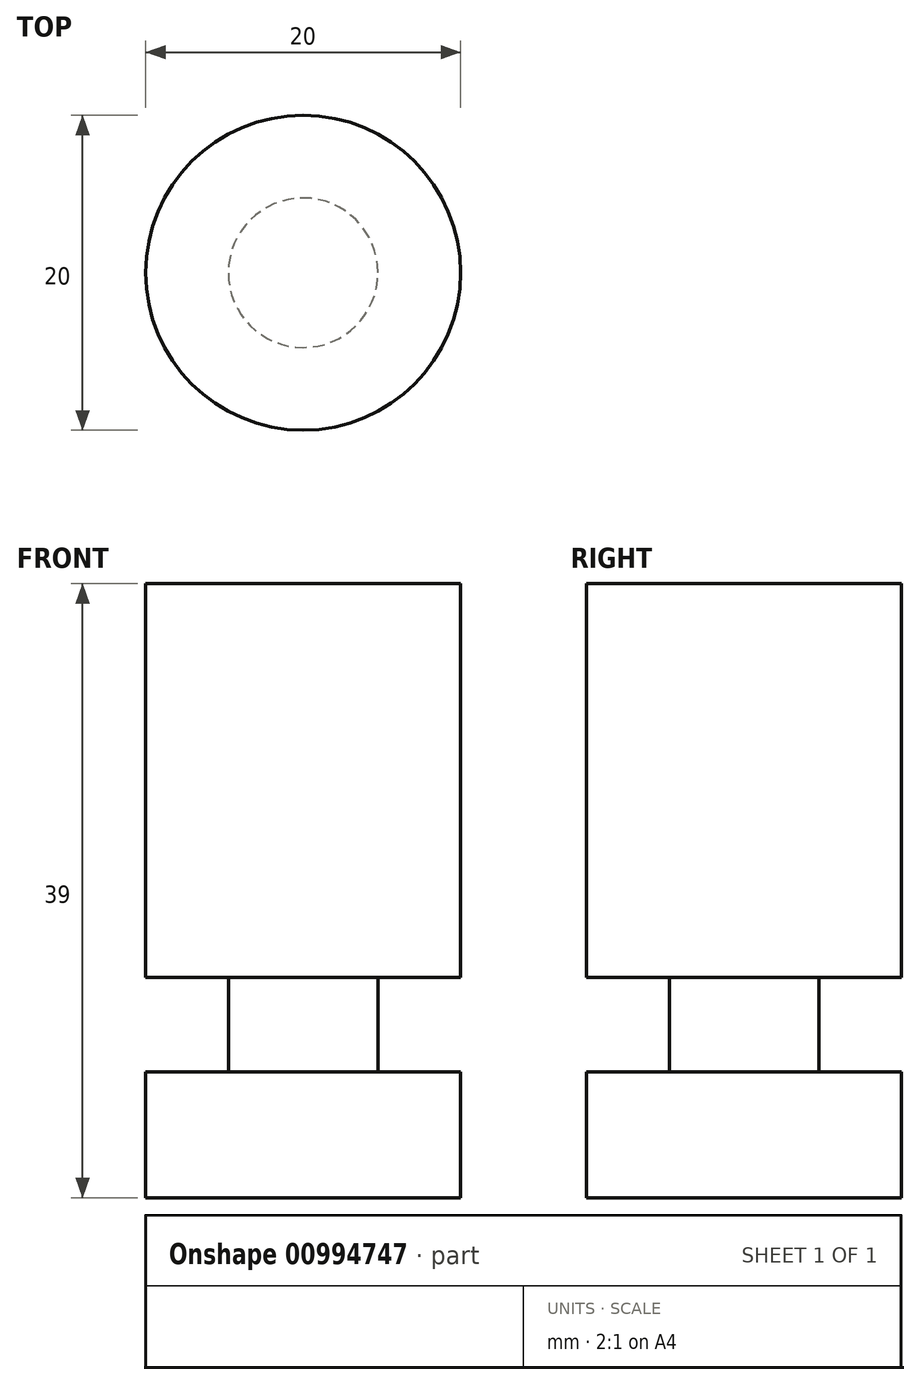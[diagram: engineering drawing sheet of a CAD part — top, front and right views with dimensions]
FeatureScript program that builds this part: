
annotation { "Feature Type Name" : "Feature", "Feature Type Description" : "" }
export const myFeature = defineFeature(function(context is Context, id is Id, definition is map)
    precondition{}
    {
        {
            var Q0;
            Q0=qCreatedBy(makeId("Top.planeOp"),FACE);
            var sketch = newSketch(context, id + "F0", { "sketchPlane" : qUnion([Q0])});
            skCircle(sketch, "E0", {"center": v(0, 0) * mm, "radius": 10 * mm});
            skCircle(sketch, "E1", {"center": v(0, 0) * mm, "radius": 4.75 * mm});
            skSolve(sketch);
        }
        {
            var Q0;
            Q0=makeQuery(id+"F0.imprint","IMPRINT",FACE,{"disambiguationData":[TD([[makeQuery(id+"F0.imprint","IMPRINT",EDGE,{"derivedFrom":sQuery(id+"F0.wireOp",EDGE,"E0")}),1.0]])]});
            var Q1;
            Q1=makeQuery(id+"F0.imprint","IMPRINT",FACE,{"disambiguationData":[TD([[makeQuery(id+"F0.imprint","IMPRINT",EDGE,{"derivedFrom":sQuery(id+"F0.wireOp",EDGE,"E1")}),1.0]])]});
            extrude(context, id + "F1", {"entities" : qUnion([Q0, Q1]), "depth" : 25 * mm, "offsetDistance" : 25 * mm});
        }
        {
            var Q0;
            Q0=makeQuery(id+"F0.imprint","IMPRINT",FACE,{"disambiguationData":[TD([[makeQuery(id+"F0.imprint","IMPRINT",EDGE,{"derivedFrom":sQuery(id+"F0.wireOp",EDGE,"E1")}),1.0]])]});
            extrude(context, id + "F2", {"entities" : qUnion([Q0]), "operationType" : NewBodyOperationType.ADD, "oppositeDirection" : true, "depth" : 6 * mm, "offsetDistance" : 25 * mm});
        }
        {
            var Q0;
            Q0=makeQuery(id+"F2.opExtrude","CAP_FACE",FACE,{"disambiguationData":[OSD([sQuery(id+"F0.wireOp",EDGE,"E1")])],"isStart":false});
            var sketch = newSketch(context, id + "F3", { "sketchPlane" : qUnion([Q0])});
            skCircle(sketch, "E2", {"center": v(0, 0) * mm, "radius": 10 * mm});
            skSolve(sketch);
        }
        {
            var Q0;
            Q0 = qSketchRegion(id + "F3", true);
            extrude(context, id + "F4", {"entities" : qUnion([Q0]), "operationType" : NewBodyOperationType.ADD, "depth" : 8 * mm, "offsetDistance" : 25 * mm});
        }
    });
